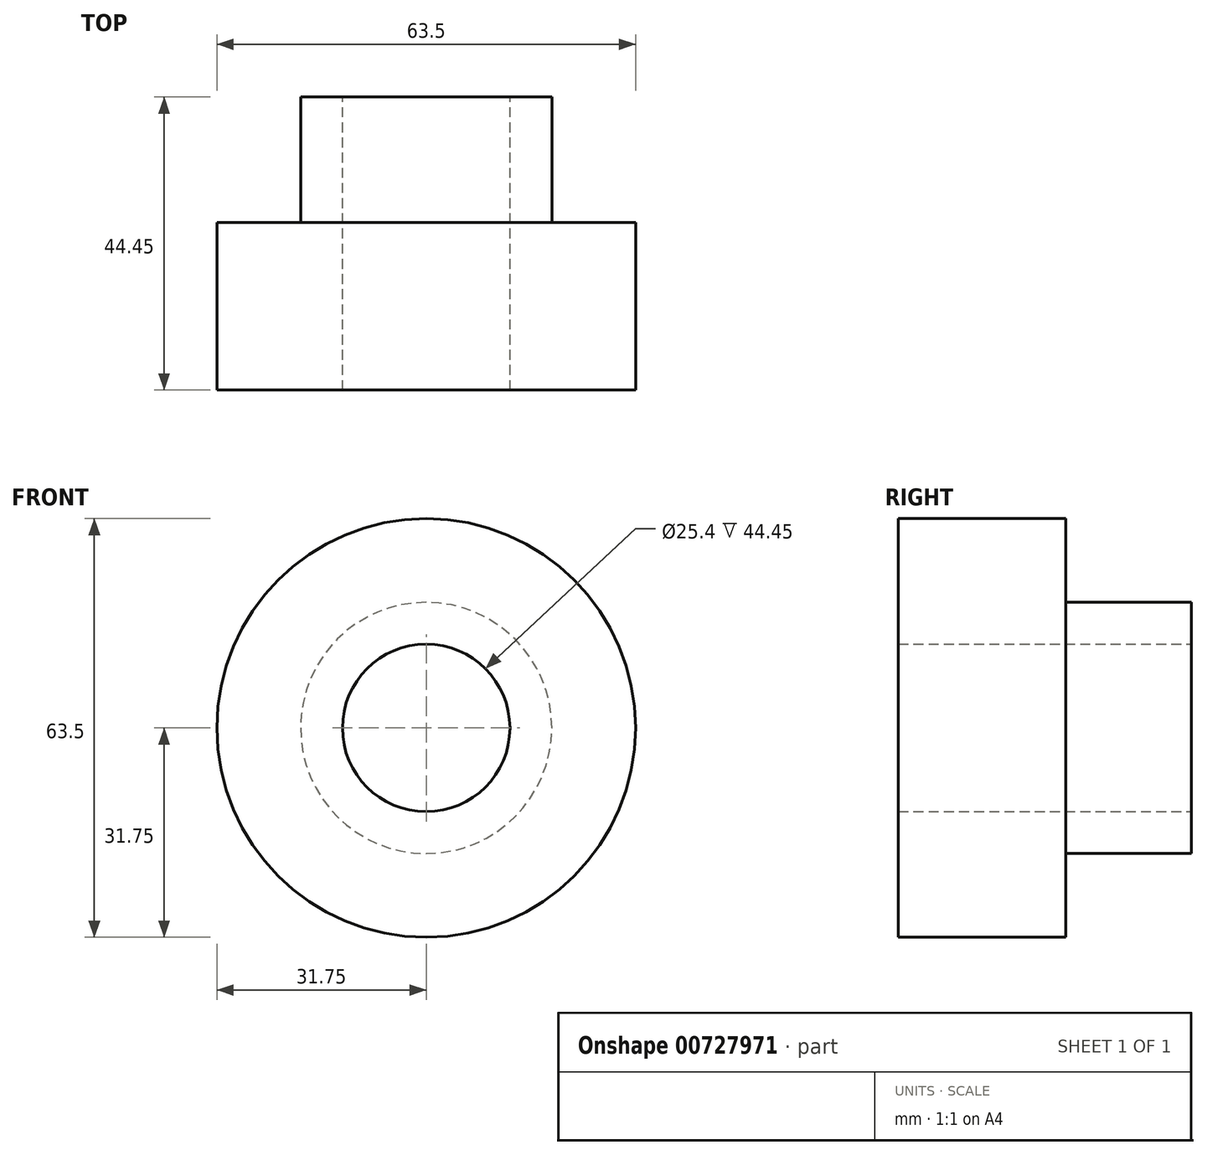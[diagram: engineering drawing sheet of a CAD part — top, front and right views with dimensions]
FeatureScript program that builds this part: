
annotation { "Feature Type Name" : "Feature", "Feature Type Description" : "" }
export const myFeature = defineFeature(function(context is Context, id is Id, definition is map)
    precondition{}
    {
        {
            var Q0;
            Q0=qCreatedBy(makeId("Front.planeOp"),FACE);
            var sketch = newSketch(context, id + "F0", { "sketchPlane" : qUnion([Q0])});
            skCircle(sketch, "E0", {"center": v(0, 0) * mm, "radius": 12.7 * mm});
            skCircle(sketch, "E1", {"center": v(0, 0) * mm, "radius": 31.75 * mm});
            skSolve(sketch);
        }
        {
            var Q0;
            Q0=makeQuery(id+"F0.imprint","IMPRINT",FACE,{"disambiguationData":[TD([[makeQuery(id+"F0.imprint","IMPRINT",EDGE,{"derivedFrom":sQuery(id+"F0.wireOp",EDGE,"E0")}),-1.0]])]});
            extrude(context, id + "F1", {"entities" : qUnion([Q0]), "depth" : 25.4 * mm, "offsetDistance" : 25.4 * mm});
        }
        {
            var Q0;
            Q0=qCreatedBy(makeId("Front.planeOp"),FACE);
            var sketch = newSketch(context, id + "F2", { "sketchPlane" : qUnion([Q0])});
            skCircle(sketch, "E2", {"center": v(0, 0) * mm, "radius": 19.05 * mm});
            skCircle(sketch, "E3", {"center": v(0, 0) * mm, "radius": 12.7 * mm});
            skSolve(sketch);
        }
        {
            var Q0;
            Q0=makeQuery(id+"F2.imprint","IMPRINT",FACE,{"disambiguationData":[TD([[makeQuery(id+"F2.imprint","IMPRINT",EDGE,{"derivedFrom":sQuery(id+"F2.wireOp",EDGE,"E2")}),1.0]])]});
            extrude(context, id + "F3", {"entities" : qUnion([Q0]), "operationType" : NewBodyOperationType.ADD, "oppositeDirection" : true, "depth" : 19.05 * mm, "offsetDistance" : 25.4 * mm});
        }
    });
